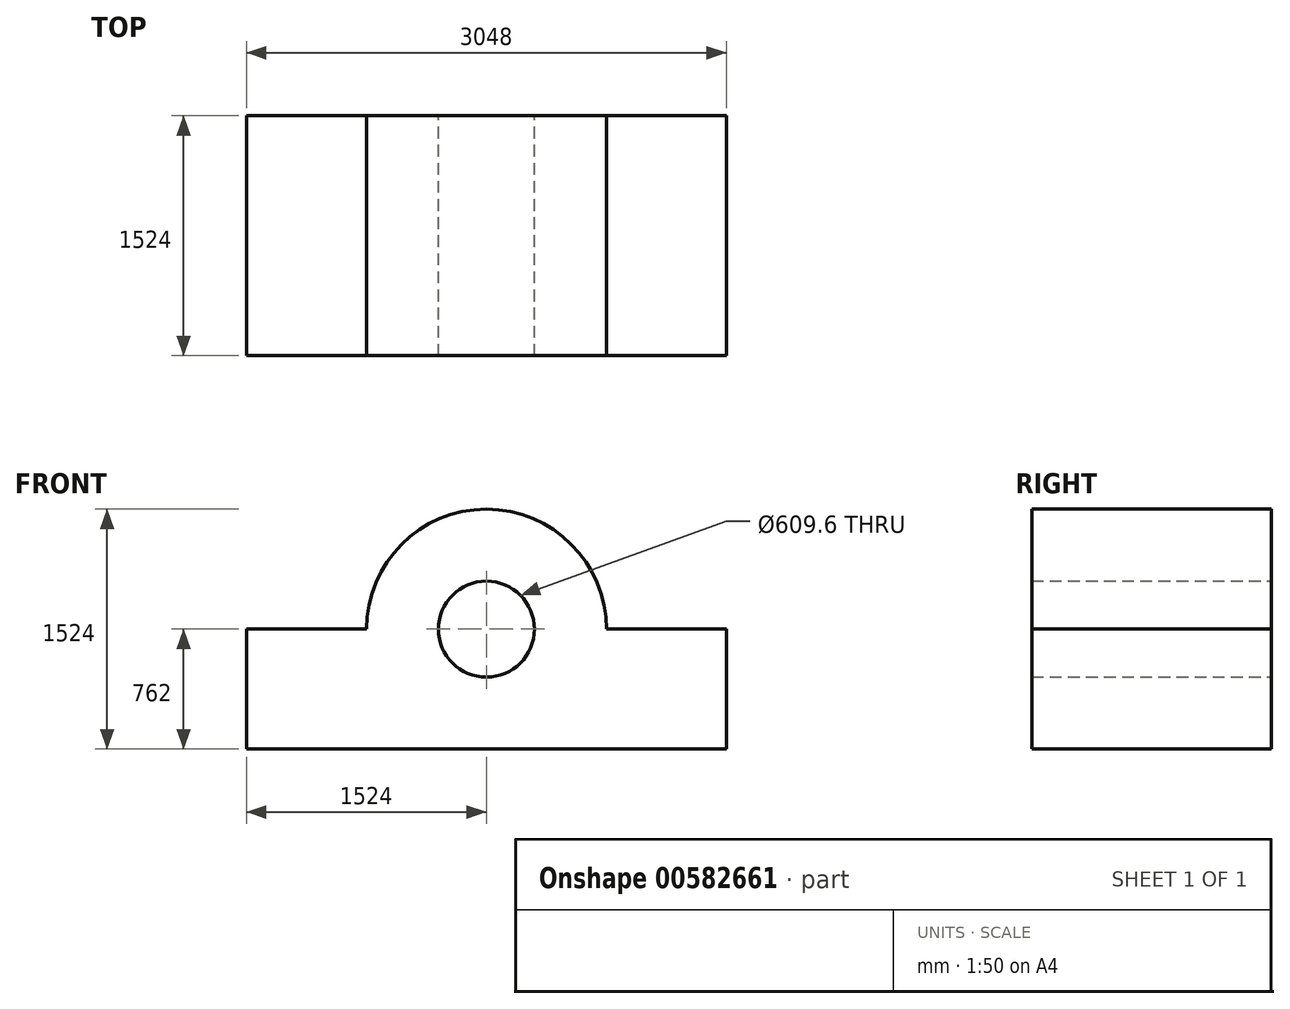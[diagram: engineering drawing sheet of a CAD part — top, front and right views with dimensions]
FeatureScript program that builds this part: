
annotation { "Feature Type Name" : "Feature", "Feature Type Description" : "" }
export const myFeature = defineFeature(function(context is Context, id is Id, definition is map)
    precondition{}
    {
        {
            var Q0;
            Q0=qCreatedBy(makeId("Front.planeOp"),FACE);
            var sketch = newSketch(context, id + "F0", { "sketchPlane" : qUnion([Q0])});
            skCircle(sketch, "E0", {"center": v(0, 0) * mm, "radius": 304.8 * mm});
            skArc(sketch, "E1", {"start": v(762, 0) * mm, "mid": v(0, 762) * mm, "end": v(-762, 0) * mm});
            skLineSegment(sketch, "E2", {"start": v(762, 0) * mm, "end": v(1524, 0) * mm});
            skLineSegment(sketch, "E3", {"start": v(1524, 0) * mm, "end": v(1524, -762) * mm});
            skLineSegment(sketch, "E4", {"start": v(-1524, 0) * mm, "end": v(-1524, -762) * mm});
            skLineSegment(sketch, "E5", {"start": v(-1524, -762) * mm, "end": v(1524, -762) * mm});
            skLineSegment(sketch, "E6.trimOffspring", {"start": v(-762, 0) * mm, "end": v(-1524, 0) * mm});
            skSolve(sketch);
        }
        {
            var Q0;
            Q0=makeQuery(id+"F0.imprint","IMPRINT",FACE,{"disambiguationData":[TD([[makeQuery(id+"F0.imprint","IMPRINT",EDGE,{"derivedFrom":sQuery(id+"F0.wireOp",EDGE,"E0")}),-1.0]])]});
            extrude(context, id + "F1", {"entities" : qUnion([Q0]), "depth" : 1524 * mm, "offsetDistance" : 25.4 * mm, "symmetric" : true});
        }
    });
